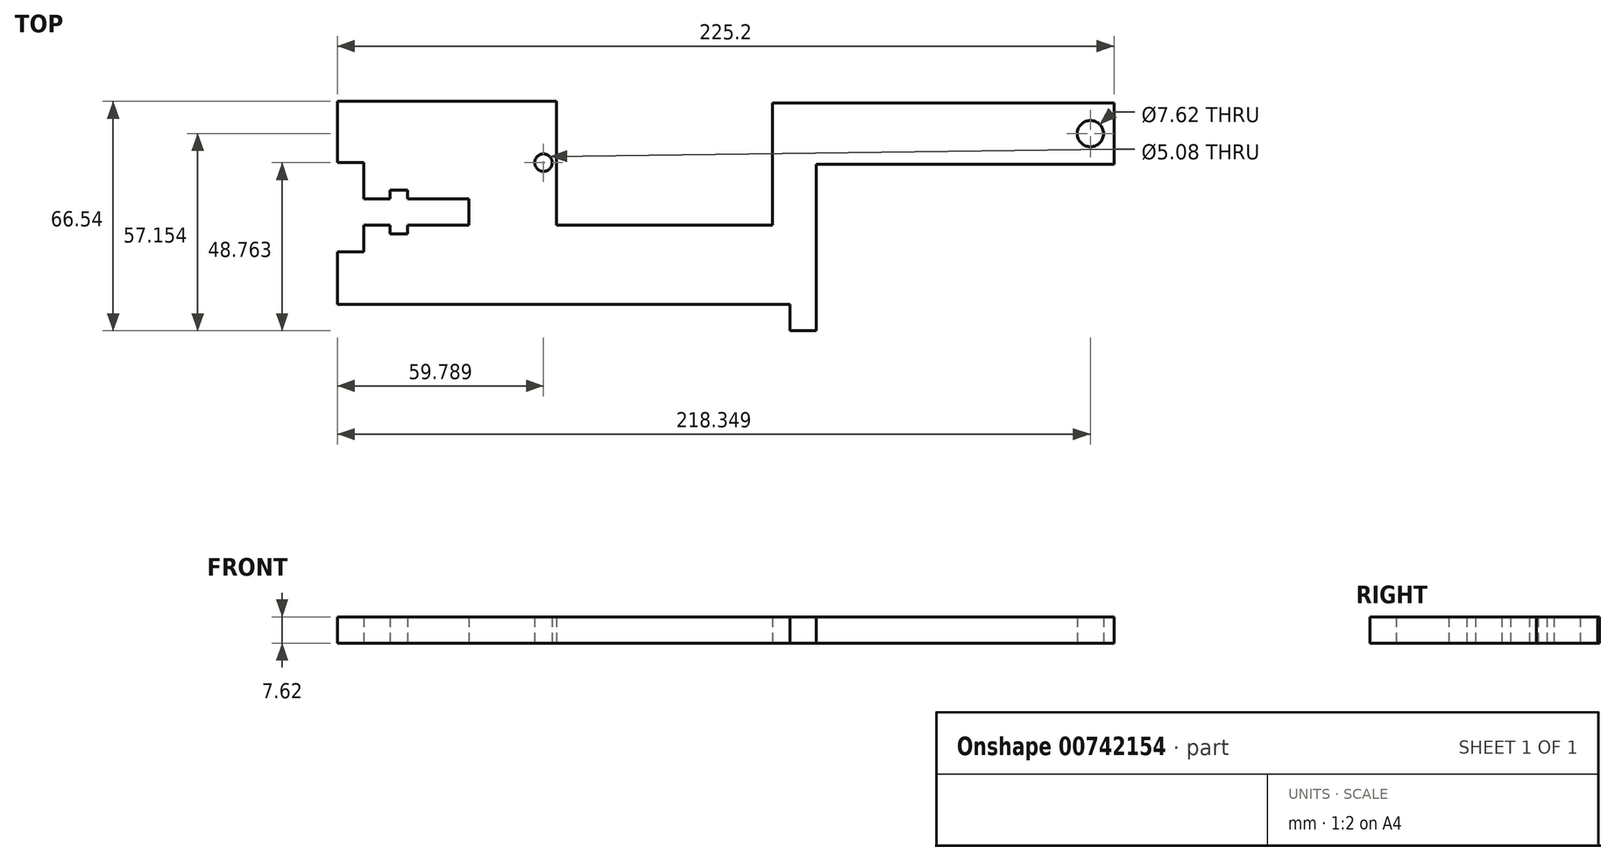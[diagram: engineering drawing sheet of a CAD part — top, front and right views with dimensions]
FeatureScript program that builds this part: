
annotation { "Feature Type Name" : "Feature", "Feature Type Description" : "" }
export const myFeature = defineFeature(function(context is Context, id is Id, definition is map)
    precondition{}
    {
        {
            var Q0;
            Q0=qCreatedBy(makeId("Top.planeOp"),FACE);
            var sketch = newSketch(context, id + "F0", { "sketchPlane" : qUnion([Q0])});
            skLineSegment(sketch, "E0.bottom", {"start": v(-16.88, 29.95) * mm, "end": v(82.18, 29.95) * mm});
            skLineSegment(sketch, "E0.left", {"start": v(-16.88, 29.95) * mm, "end": v(-16.88, 12.17) * mm});
            skLineSegment(sketch, "E0.right", {"start": v(82.18, 29.95) * mm, "end": v(82.18, 12.17) * mm});
            skLineSegment(sketch, "E1.bottom", {"start": v(-16.88, 29.95) * mm, "end": v(-4.18, 29.95) * mm});
            skLineSegment(sketch, "E1.top", {"start": v(-16.88, -28.47) * mm, "end": v(-4.18, -28.47) * mm});
            skLineSegment(sketch, "E2.left", {"start": v(-4.18, -28.47) * mm, "end": v(-4.18, -5.51) * mm});
            skLineSegment(sketch, "E3", {"start": v(-135.4, -28.47) * mm, "end": v(-4.18, -28.47) * mm});
            skLineSegment(sketch, "E4", {"start": v(-135.4, -13.23) * mm, "end": v(-143.02, -13.23) * mm});
            skLineSegment(sketch, "E5", {"start": v(-143.02, -13.23) * mm, "end": v(-143.02, -28.47) * mm});
            skLineSegment(sketch, "E6", {"start": v(-143.02, -28.47) * mm, "end": v(-135.4, -28.47) * mm});
            skLineSegment(sketch, "E7.top", {"start": v(-143.02, 30.45) * mm, "end": v(-79.52, 30.45) * mm});
            skLineSegment(sketch, "E7.right", {"start": v(-79.52, 5.05) * mm, "end": v(-79.52, 30.45) * mm});
            skLineSegment(sketch, "E8.top", {"start": v(-143.02, 12.67) * mm, "end": v(-135.4, 12.67) * mm});
            skLineSegment(sketch, "E9.bottom", {"start": v(-135.4, -5.51) * mm, "end": v(-127.78, -5.51) * mm});
            skLineSegment(sketch, "E10.top", {"start": v(-127.78, -8.05) * mm, "end": v(-122.7, -8.05) * mm});
            skLineSegment(sketch, "E10.left", {"start": v(-127.78, -5.51) * mm, "end": v(-127.78, -8.05) * mm});
            skLineSegment(sketch, "E10.right", {"start": v(-122.7, -5.51) * mm, "end": v(-122.7, -8.05) * mm});
            skLineSegment(sketch, "E11.top", {"start": v(-127.78, 4.65) * mm, "end": v(-122.7, 4.65) * mm});
            skLineSegment(sketch, "E11.left", {"start": v(-127.78, 4.65) * mm, "end": v(-127.78, 5.05) * mm});
            skLineSegment(sketch, "E11.right", {"start": v(-122.7, 2.1) * mm, "end": v(-122.7, 4.65) * mm});
            skLineSegment(sketch, "E12.left", {"start": v(-79.52, 2.1) * mm, "end": v(-79.52, 5.05) * mm});
            skLineSegment(sketch, "E13", {"start": v(-122.7, 2.1) * mm, "end": v(-104.92, 2.1) * mm});
            skLineSegment(sketch, "E14", {"start": v(-143.02, 30.45) * mm, "end": v(-143.02, 12.67) * mm});
            skLineSegment(sketch, "E15", {"start": v(-135.4, -5.51) * mm, "end": v(-135.4, -13.23) * mm});
            skLineSegment(sketch, "E16.bottom", {"start": v(-4.18, -28.47) * mm, "end": v(-11.8, -28.47) * mm});
            skLineSegment(sketch, "E16.top", {"start": v(-4.18, -36.09) * mm, "end": v(-11.8, -36.09) * mm});
            skLineSegment(sketch, "E16.left", {"start": v(-4.18, -28.47) * mm, "end": v(-4.18, -36.09) * mm});
            skLineSegment(sketch, "E16.right", {"start": v(-11.8, -28.47) * mm, "end": v(-11.8, -36.09) * mm});
            skLineSegment(sketch, "E17", {"start": v(-135.4, 12.67) * mm, "end": v(-135.4, 2.1) * mm});
            skLineSegment(sketch, "E18", {"start": v(-135.4, 2.1) * mm, "end": v(-127.78, 2.1) * mm});
            skLineSegment(sketch, "E19", {"start": v(-127.78, 2.1) * mm, "end": v(-127.78, 4.65) * mm});
            skCircle(sketch, "E20", {"center": v(-83.23, 12.67) * mm, "radius": 2.54 * mm});
            skCircle(sketch, "E21", {"center": v(75.33, 21.06) * mm, "radius": 3.81 * mm});
            skPoint(sketch, "E21.centerSnap0", {"position": v(82.18, 21.06) * mm});
            skLineSegment(sketch, "E22", {"start": v(82.18, 12.17) * mm, "end": v(-4.18, 12.17) * mm});
            skLineSegment(sketch, "E23", {"start": v(-4.18, 12.17) * mm, "end": v(-4.18, -5.51) * mm});
            skLineSegment(sketch, "E24", {"start": v(-16.88, 12.17) * mm, "end": v(-16.88, -5.51) * mm});
            skLineSegment(sketch, "E25", {"start": v(-104.92, 2.1) * mm, "end": v(-104.92, -5.51) * mm});
            skLineSegment(sketch, "E26", {"start": v(-79.52, 2.1) * mm, "end": v(-79.52, -5.51) * mm});
            skLineSegment(sketch, "E27", {"start": v(-122.7, -5.51) * mm, "end": v(-104.92, -5.51) * mm});
            skLineSegment(sketch, "E28", {"start": v(-79.52, -5.51) * mm, "end": v(-16.88, -5.51) * mm});
            skSolve(sketch);
        }
        {
            var Q0;
            Q0 = qSketchRegion(id + "F0", true);
            extrude(context, id + "F1", {"entities" : qUnion([Q0]), "depth" : 7.62 * mm, "offsetDistance" : 25.4 * mm});
        }
    });
